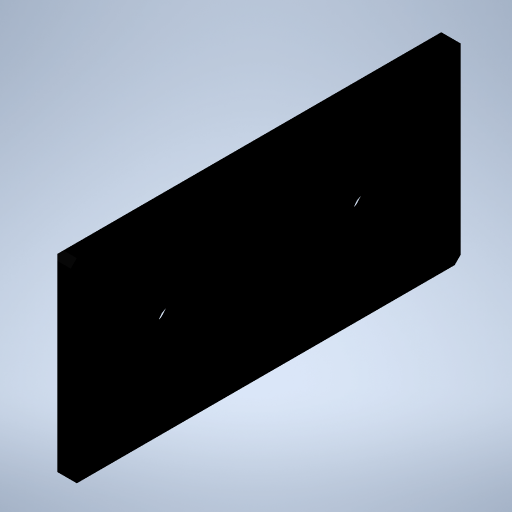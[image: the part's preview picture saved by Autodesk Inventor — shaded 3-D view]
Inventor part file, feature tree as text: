
AUTODESK INVENTOR PART (.ipt)
format: ipt  version: 2023 (Build 270158000, 158)  size: 262,656 bytes
history: native  units: mm
features: other x98, sketch x3, hole x2, extrude x1, chamfer x1
ambient origin geometry x8: Origin, YZ Plane, XZ Plane, XY Plane, X Axis, Y Axis, Z Axis, Center Point
bodies: Solid1 (feature_tree)
feature tree (105):
  extrude  "Extrusion1"  TaperAngle=0.0deg  [1 undecoded]
  hole  "Hole1"  [1 undecoded]
  hole  "Hole2"  [1 undecoded]
  other  "CS_ANBAU_CAP_XY"
  other  "CS_ANBAU_CAP_YZ"
  other  "CS_ANBAU_CAP_ZX"
  other  "CS_ANBAU_CAP_X"
  other  "CS_ANBAU_CAP_Y"
  other  "CS_ANBAU_CAP_Z"
  other  "CS_ANBAU_CAP_Center"
  other  "CS_ANBAU_CAP_90_XY"
  other  "CS_ANBAU_CAP_90_YZ"
  other  "CS_ANBAU_CAP_90_ZX"
  other  "CS_ANBAU_CAP_90_X"
  other  "CS_ANBAU_CAP_90_Y"
  other  "CS_ANBAU_CAP_90_Z"
  other  "CS_ANBAU_CAP_90_Center"
  other  "IB_1_XY"
  other  "IB_1_YZ"
  other  "IB_1_ZX"
  other  "IB_1_X"
  other  "IB_1_Y"
  other  "IB_1_Z"
  other  "IB_1_Center"
  other  "IB_10_XY"
  other  "IB_10_YZ"
  other  "IB_10_ZX"
  other  "IB_10_X"
  other  "IB_10_Y"
  other  "IB_10_Z"
  other  "IB_10_Center"
  other  "IB_11_XY"
  other  "IB_11_YZ"
  other  "IB_11_ZX"
  other  "IB_11_X"
  other  "IB_11_Y"
  other  "IB_11_Z"
  other  "IB_11_Center"
  other  "IB_12_XY"
  other  "IB_12_YZ"
  other  "IB_12_ZX"
  other  "IB_12_X"
  other  "IB_12_Y"
  other  "IB_12_Z"
  other  "IB_12_Center"
  other  "IB_2_XY"
  other  "IB_2_YZ"
  other  "IB_2_ZX"
  other  "IB_2_X"
  other  "IB_2_Y"
  other  "IB_2_Z"
  other  "IB_2_Center"
  other  "IB_3_XY"
  other  "IB_3_YZ"
  other  "IB_3_ZX"
  other  "IB_3_X"
  other  "IB_3_Y"
  other  "IB_3_Z"
  other  "IB_3_Center"
  other  "IB_4_XY"
  other  "IB_4_YZ"
  other  "IB_4_ZX"
  other  "IB_4_X"
  other  "IB_4_Y"
  other  "IB_4_Z"
  other  "IB_4_Center"
  other  "IB_5_XY"
  other  "IB_5_YZ"
  other  "IB_5_ZX"
  other  "IB_5_X"
  other  "IB_5_Y"
  other  "IB_5_Z"
  other  "IB_5_Center"
  other  "IB_6_XY"
  other  "IB_6_YZ"
  other  "IB_6_ZX"
  other  "IB_6_X"
  other  "IB_6_Y"
  other  "IB_6_Z"
  other  "IB_6_Center"
  other  "IB_7_XY"
  other  "IB_7_YZ"
  other  "IB_7_ZX"
  other  "IB_7_X"
  other  "IB_7_Y"
  other  "IB_7_Z"
  other  "IB_7_Center"
  other  "IB_8_XY"
  other  "IB_8_YZ"
  other  "IB_8_ZX"
  other  "IB_8_X"
  other  "IB_8_Y"
  other  "IB_8_Z"
  other  "IB_8_Center"
  other  "IB_9_XY"
  other  "IB_9_YZ"
  other  "IB_9_ZX"
  other  "IB_9_X"
  other  "IB_9_Y"
  other  "IB_9_Z"
  other  "IB_9_Center"
  chamfer  "Chamfer1"  [1 undecoded]
  sketch  "Skizze_1"  dims[d0=4.0mm d1=0.0mm]
  sketch  "Sketch2"  dims[d2=4.0mm d3=6.0mm d4=8.1mm d5=2.0mm d6=90.0deg d7=4.0mm d8=0.0mm]
  sketch  "Sketch3"  dims[d9=4.0mm d10=6.0mm d11=8.1mm d12=2.0mm d13=90.0deg d14=4.0mm d15=0.0mm d16=0.0mm d17=0.0mm d18=0.0mm d19=0.0mm d20=0.0mm d21=0.0mm d22=0.0mm d23=0.0mm d24=0.0mm d25=0.0mm d26=0.0mm d27=0.0mm d28=1.25mm d29=2.0mm d30=45.0deg]
note: 4 required parameter values undecoded (feature->parameter linkage not recoverable at this tier; creation-order binding heuristic only, values carry confidence <= 0.55)
